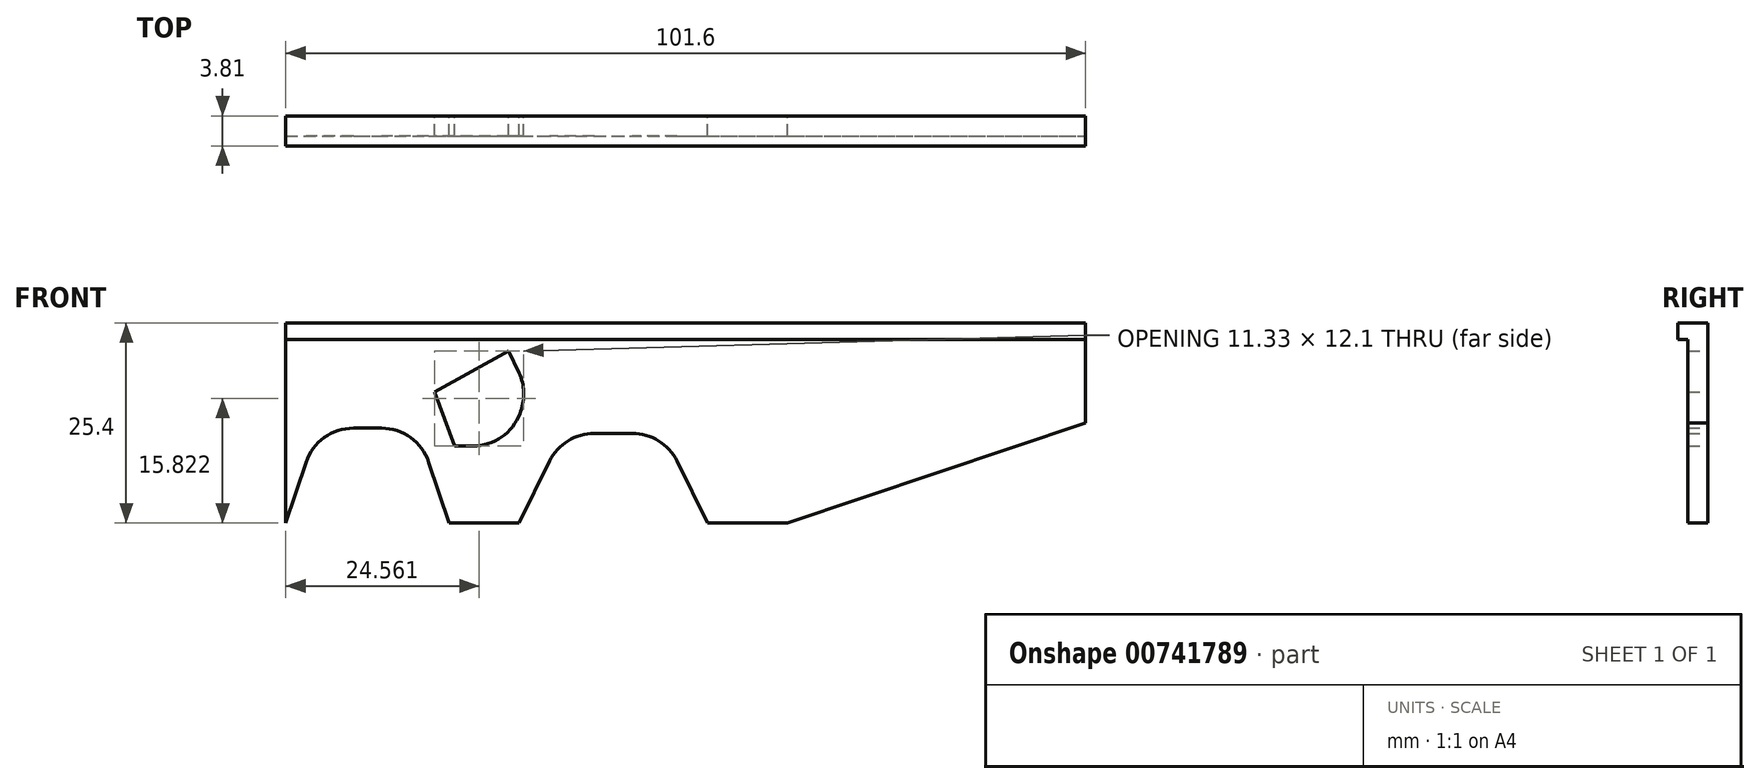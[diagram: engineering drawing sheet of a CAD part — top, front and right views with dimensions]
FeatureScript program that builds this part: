
annotation { "Feature Type Name" : "Feature", "Feature Type Description" : "" }
export const myFeature = defineFeature(function(context is Context, id is Id, definition is map)
    precondition{}
    {
        {
            var Q0;
            Q0=qCreatedBy(makeId("Front.planeOp"),FACE);
            var sketch = newSketch(context, id + "F0", { "sketchPlane" : qUnion([Q0])});
            skLineSegment(sketch, "E0.bottom", {"start": v(-46.8, 10.61) * mm, "end": v(54.8, 10.61) * mm});
            skLineSegment(sketch, "E0.top", {"start": v(-46.8, -14.79) * mm, "end": v(54.8, -14.79) * mm});
            skLineSegment(sketch, "E0.left", {"start": v(-46.8, 10.61) * mm, "end": v(-46.8, -14.79) * mm});
            skLineSegment(sketch, "E0.right", {"start": v(54.8, 10.61) * mm, "end": v(54.8, -14.79) * mm});
            skLineSegment(sketch, "E1", {"start": v(-46.8, -14.79) * mm, "end": v(-44.23, -7.08) * mm});
            skLineSegment(sketch, "E2", {"start": v(-38.2, -2.74) * mm, "end": v(-34.65, -2.74) * mm});
            skLineSegment(sketch, "E3", {"start": v(-28.63, -7.08) * mm, "end": v(-26.05, -14.79) * mm});
            skLineSegment(sketch, "E4", {"start": v(-17.16, -14.79) * mm, "end": v(-13.29, -6.94) * mm});
            skLineSegment(sketch, "E5", {"start": v(-7.6, -3.4) * mm, "end": v(-2.78, -3.4) * mm});
            skLineSegment(sketch, "E6", {"start": v(2.9, -6.94) * mm, "end": v(6.79, -14.79) * mm});
            skLineSegment(sketch, "E7", {"start": v(16.95, -14.79) * mm, "end": v(54.8, -2.09) * mm});
            skLineSegment(sketch, "E8", {"start": v(-46.8, 8.51) * mm, "end": v(54.8, 8.51) * mm});
            skLineSegment(sketch, "E9", {"start": v(-27.9, 1.88) * mm, "end": v(-25.36, -5.02) * mm});
            skLineSegment(sketch, "E10", {"start": v(-25.36, -5.02) * mm, "end": v(-23.01, -5.02) * mm});
            skLineSegment(sketch, "E11", {"start": v(-17.06, -0.86) * mm, "end": v(-16.96, -0.6) * mm});
            skLineSegment(sketch, "E12", {"start": v(-17.16, 4.27) * mm, "end": v(-18.47, 7.08) * mm});
            skLineSegment(sketch, "E13", {"start": v(-18.47, 7.08) * mm, "end": v(-27.9, 1.88) * mm});
            skPoint(sketch, "E14.visualSharp", {"position": v(-42.78, -2.74) * mm});
            skArc(sketch, "E14.filletArc", {"start": v(-38.2, -2.74) * mm, "mid": v(-41.91, -3.94) * mm, "end": v(-44.23, -7.08) * mm});
            skPoint(sketch, "E15.visualSharp", {"position": v(-30.08, -2.74) * mm});
            skArc(sketch, "E15.filletArc", {"start": v(-28.63, -7.08) * mm, "mid": v(-30.94, -3.94) * mm, "end": v(-34.65, -2.74) * mm});
            skPoint(sketch, "E16.visualSharp", {"position": v(-11.54, -3.4) * mm});
            skArc(sketch, "E16.filletArc", {"start": v(-7.6, -3.4) * mm, "mid": v(-10.94, -4.36) * mm, "end": v(-13.29, -6.94) * mm});
            skPoint(sketch, "E17.visualSharp", {"position": v(1.16, -3.4) * mm});
            skArc(sketch, "E17.filletArc", {"start": v(2.9, -6.94) * mm, "mid": v(0.57, -4.36) * mm, "end": v(-2.78, -3.4) * mm});
            skPoint(sketch, "E18.visualSharp", {"position": v(-16.05, 1.88) * mm});
            skArc(sketch, "E18.filletArc", {"start": v(-16.96, -0.6) * mm, "mid": v(-16.57, 1.86) * mm, "end": v(-17.16, 4.27) * mm});
            skPoint(sketch, "E19.visualSharp", {"position": v(-18.59, -5.02) * mm});
            skArc(sketch, "E19.filletArc", {"start": v(-23.01, -5.02) * mm, "mid": v(-19.38, -3.88) * mm, "end": v(-17.06, -0.86) * mm});
            skSolve(sketch);
        }
        {
            var Q0;
            {var subQ2=sQuery(id+"F0.wireOp",EDGE,"E1");Q0=makeQuery(id+"F0.imprint","IMPRINT",FACE,{"disambiguationData":[TD([[makeQuery(id+"F0.imprint","IMPRINT",EDGE,{"derivedFrom":subQ2}),1.0]])]});}
            extrude(context, id + "F1", {"entities" : qUnion([Q0]), "depth" : 2.54 * mm, "offsetDistance" : 25.4 * mm});
        }
        {
            var Q0;
            {var subQ0=sQuery(id+"F0.wireOp",EDGE,"E0.bottom");Q0=makeQuery(id+"F0.imprint","IMPRINT",FACE,{"disambiguationData":[TD([[makeQuery(id+"F0.imprint","IMPRINT",EDGE,{"derivedFrom":subQ0}),-1.0]])]});}
            extrude(context, id + "F2", {"entities" : qUnion([Q0]), "operationType" : NewBodyOperationType.ADD, "depth" : 3.8 * mm, "offsetDistance" : 25.4 * mm});
        }
    });
